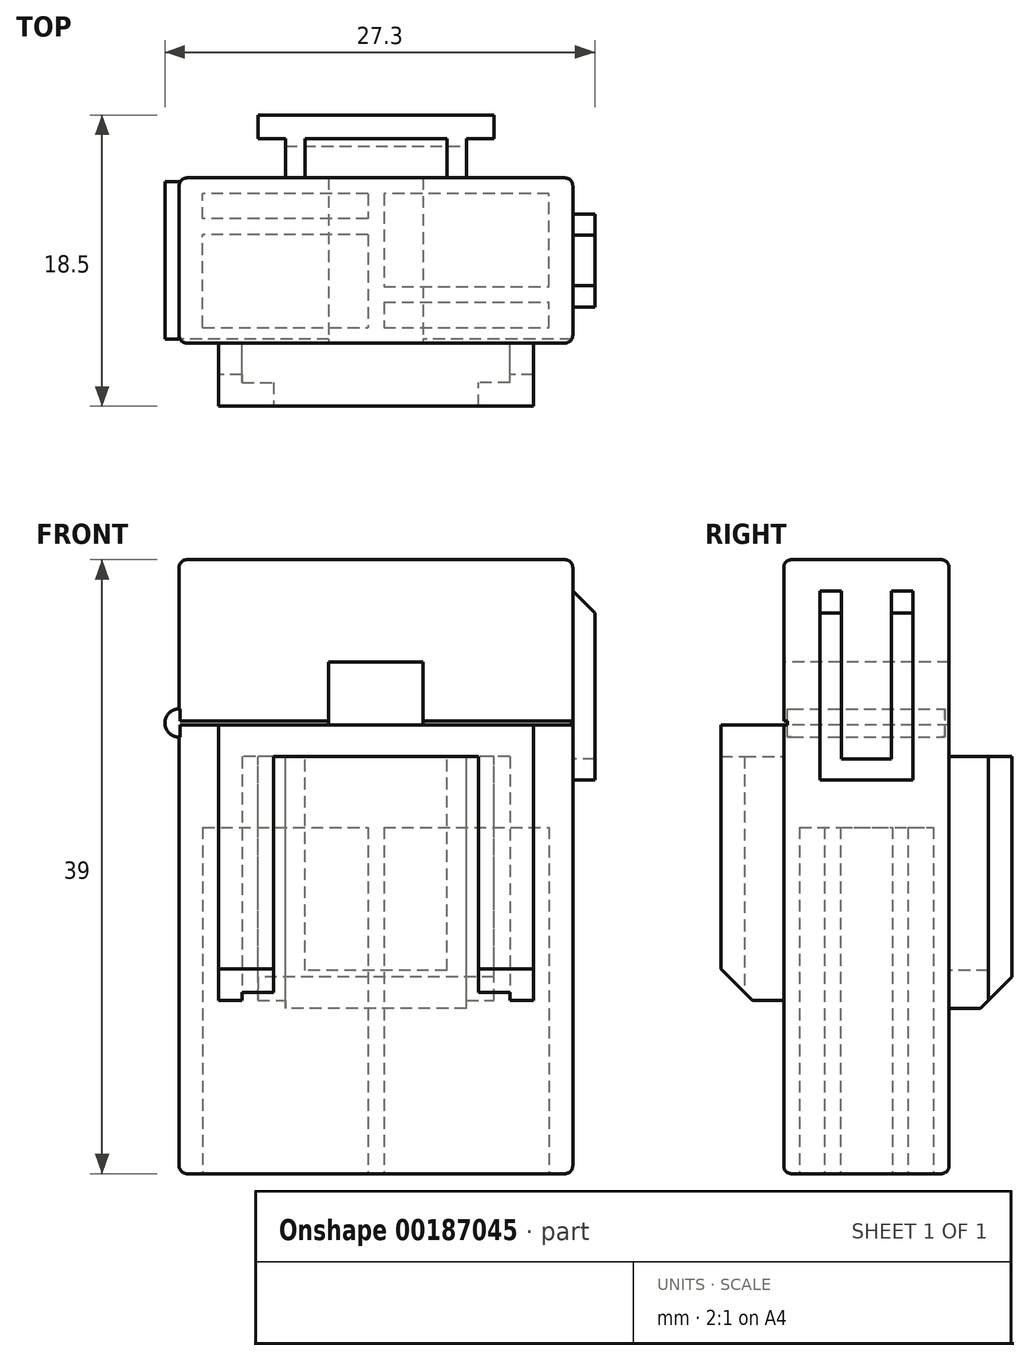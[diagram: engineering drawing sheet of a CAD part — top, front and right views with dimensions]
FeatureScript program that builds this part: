
annotation { "Feature Type Name" : "Feature", "Feature Type Description" : "" }
export const myFeature = defineFeature(function(context is Context, id is Id, definition is map)
    precondition{}
    {
        {
            var Q0;
            Q0=qCreatedBy(makeId("Front.planeOp"),FACE);
            var sketch = newSketch(context, id + "F0", { "sketchPlane" : qUnion([Q0])});
            skLineSegment(sketch, "E0.bottom", {"start": v(12.5, 19.5) * mm, "end": v(-12.5, 19.5) * mm});
            skLineSegment(sketch, "E0.top", {"start": v(12.5, -19.5) * mm, "end": v(-12.5, -19.5) * mm});
            skLineSegment(sketch, "E0.left", {"start": v(12.5, 19.5) * mm, "end": v(12.5, -19.5) * mm});
            skLineSegment(sketch, "E0.right", {"start": v(-12.5, 19.5) * mm, "end": v(-12.5, -19.5) * mm});
            skPoint(sketch, "E0.middle", {"position": v(0, 0) * mm});
            skSolve(sketch);
        }
        {
            var Q0;
            Q0=makeQuery(id+"F0.imprint","IMPRINT",FACE,{"disambiguationData":[TD([[makeQuery(id+"F0.imprint","IMPRINT",EDGE,{"derivedFrom":sQuery(id+"F0.wireOp",EDGE,"E0.bottom")}),1.0]])]});
            extrude(context, id + "F1", {"entities" : qUnion([Q0]), "endBound" : BoundingType.SYMMETRIC, "depth" : 10.5 * mm});
        }
        {
            var Q0;
            Q0=makeQuery(id+"F1.opExtrude","CAP_FACE",FACE,{"disambiguationData":[OSD([sQuery(id+"F0.wireOp",EDGE,"E0.bottom"),sQuery(id+"F0.wireOp",EDGE,"E0.top"),sQuery(id+"F0.wireOp",EDGE,"E0.left"),sQuery(id+"F0.wireOp",EDGE,"E0.right")])],"isStart":false});
            var sketch = newSketch(context, id + "F2", { "sketchPlane" : qUnion([Q0])});
            skLineSegment(sketch, "E1.0", {"start": v(10, 9) * mm, "end": v(-10, 9) * mm});
            skLineSegment(sketch, "E2.0", {"start": v(10, 9) * mm, "end": v(10, -8.5) * mm});
            skLineSegment(sketch, "E3.0", {"start": v(-10, 9) * mm, "end": v(-10, -8.5) * mm});
            skLineSegment(sketch, "E4.0", {"start": v(6.5, 7) * mm, "end": v(-6.5, 7) * mm});
            skLineSegment(sketch, "E5.0", {"start": v(6.5, 7) * mm, "end": v(6.5, -8.5) * mm});
            skLineSegment(sketch, "E6.0", {"start": v(-6.5, 7) * mm, "end": v(-6.5, -8.5) * mm});
            skLineSegment(sketch, "E7.0", {"start": v(10, -8.5) * mm, "end": v(6.5, -8.5) * mm});
            skLineSegment(sketch, "E8.trimOffspring", {"start": v(-6.5, -8.5) * mm, "end": v(-10, -8.5) * mm});
            skSolve(sketch);
        }
        {
            var Q0;
            Q0=makeQuery(id+"F2.imprint","IMPRINT",FACE,{"disambiguationData":[TD([[makeQuery(id+"F2.imprint","IMPRINT",EDGE,{"derivedFrom":sQuery(id+"F2.wireOp",EDGE,"E1.0")}),1.0]])]});
            extrude(context, id + "F3", {"entities" : qUnion([Q0]), "operationType" : NewBodyOperationType.ADD, "depth" : 4 * mm});
        }
        {
            var Q0;
            Q0=makeQuery(id+"F3.opExtrude","SWEPT_FACE",FACE,{"disambiguationData":[OSD([sQuery(id+"F2.wireOp",EDGE,"E7.0")])]});
            var sketch = newSketch(context, id + "F4", { "sketchPlane" : qUnion([Q0])});
            skLineSegment(sketch, "E9.0", {"start": v(8.5, 7.75) * mm, "end": v(8.5, 5.25) * mm});
            skLineSegment(sketch, "E10.0", {"start": v(8.5, 7.75) * mm, "end": v(6.5, 7.75) * mm});
            skLineSegment(sketch, "E11", {"start": v(6.5, 7.75) * mm, "end": v(6.5, 5.25) * mm});
            skLineSegment(sketch, "E12", {"start": v(6.5, 5.25) * mm, "end": v(8.5, 5.25) * mm});
            skLineSegment(sketch, "E13", {"start": v(8.5, 5.25) * mm, "end": v(6.5, 5.25) * mm});
            skLineSegment(sketch, "E14.MirrorCS", {"start": v(-8.5, 7.75) * mm, "end": v(-6.5, 7.75) * mm});
            skLineSegment(sketch, "E15.MirrorCS", {"start": v(-6.5, 7.75) * mm, "end": v(-6.5, 5.25) * mm});
            skLineSegment(sketch, "E16.MirrorCS", {"start": v(-8.5, 7.75) * mm, "end": v(-8.5, 5.25) * mm});
            skLineSegment(sketch, "E17.MirrorCS", {"start": v(-8.5, 5.25) * mm, "end": v(-6.5, 5.25) * mm});
            skSolve(sketch);
        }
        {
            var Q0;
            Q0=makeQuery(id+"F4.imprint","IMPRINT",FACE,{"disambiguationData":[TD([[makeQuery(id+"F4.imprint","IMPRINT",EDGE,{"derivedFrom":sQuery(id+"F4.wireOp",EDGE,"E9.0")}),-1.0]])]});
            var Q1;
            Q1=makeQuery(id+"F4.imprint","IMPRINT",FACE,{"disambiguationData":[TD([[makeQuery(id+"F4.imprint","IMPRINT",EDGE,{"derivedFrom":sQuery(id+"F4.wireOp",EDGE,"E14.MirrorCS")}),-1.0]])]});
            extrude(context, id + "F5", {"entities" : qUnion([Q0, Q1]), "operationType" : NewBodyOperationType.REMOVE, "oppositeDirection" : true, "depth" : 15.5 * mm});
        }
        {
            var Q0;
            Q0=makeQuery(id+"F5.boolean.opBoolean","MERGE",FACE,{"derivedFrom":[makeQuery(id+"F1.opExtrude","CAP_FACE",FACE,{"disambiguationData":[OSD([sQuery(id+"F0.wireOp",EDGE,"E0.bottom"),sQuery(id+"F0.wireOp",EDGE,"E0.top"),sQuery(id+"F0.wireOp",EDGE,"E0.left"),sQuery(id+"F0.wireOp",EDGE,"E0.right")])],"isStart":false}),makeQuery(id+"F5.opExtrude","SWEPT_FACE",FACE,{"disambiguationData":[OSD([sQuery(id+"F4.wireOp",EDGE,"E13")])]}),makeQuery(id+"F5.opExtrude","SWEPT_FACE",FACE,{"disambiguationData":[OSD([sQuery(id+"F4.wireOp",EDGE,"E17.MirrorCS")])]})]});
            var sketch = newSketch(context, id + "F6", { "sketchPlane" : qUnion([Q0])});
            skLineSegment(sketch, "E18.0", {"start": v(3, 13) * mm, "end": v(-3, 13) * mm});
            skLineSegment(sketch, "E19", {"start": v(0, 9) * mm, "end": v(0, 13) * mm});
            skLineSegment(sketch, "E20.0", {"start": v(3, 9) * mm, "end": v(3, 13) * mm});
            skLineSegment(sketch, "E21.MirrorCS", {"start": v(-3, 9) * mm, "end": v(-3, 13) * mm});
            skPoint(sketch, "E22.orphan", {"position": v(10, 13) * mm});
            skPoint(sketch, "E23.orphan", {"position": v(-10, 13) * mm});
            skLineSegment(sketch, "E24", {"start": v(-3, 9) * mm, "end": v(3, 9) * mm});
            skSolve(sketch);
        }
        {
            var Q0;
            {var subQ2=sQuery(id+"F6.wireOp",EDGE,"E19");Q0=makeQuery(id+"F6.imprint","IMPRINT",FACE,{"disambiguationData":[TD([[makeQuery(id+"F6.imprint","IMPRINT",EDGE,{"derivedFrom":subQ2}),-1.0]])]});}
            var Q1;
            {var subQ2=sQuery(id+"F6.wireOp",EDGE,"E19");Q1=makeQuery(id+"F6.imprint","IMPRINT",FACE,{"disambiguationData":[TD([[makeQuery(id+"F6.imprint","IMPRINT",EDGE,{"derivedFrom":subQ2}),1.0]])]});}
            extrude(context, id + "F7", {"entities" : qUnion([Q0, Q1]), "operationType" : NewBodyOperationType.REMOVE, "endBound" : BoundingType.THROUGH_ALL, "oppositeDirection" : true, "depth" : 25 * mm});
        }
        {
            var Q0;
            Q0=makeQuery(id+"F5.boolean.opBoolean","MERGE",FACE,{"derivedFrom":[makeQuery(id+"F1.opExtrude","CAP_FACE",FACE,{"disambiguationData":[OSD([sQuery(id+"F0.wireOp",EDGE,"E0.bottom"),sQuery(id+"F0.wireOp",EDGE,"E0.top"),sQuery(id+"F0.wireOp",EDGE,"E0.left"),sQuery(id+"F0.wireOp",EDGE,"E0.right")])],"isStart":false}),makeQuery(id+"F5.opExtrude","SWEPT_FACE",FACE,{"disambiguationData":[OSD([sQuery(id+"F4.wireOp",EDGE,"E13")])]}),makeQuery(id+"F5.opExtrude","SWEPT_FACE",FACE,{"disambiguationData":[OSD([sQuery(id+"F4.wireOp",EDGE,"E17.MirrorCS")])]})]});
            var sketch = newSketch(context, id + "F8", { "sketchPlane" : qUnion([Q0])});
            skLineSegment(sketch, "E25.0", {"start": v(12.5, 9) * mm, "end": v(-12.5, 9) * mm});
            skLineSegment(sketch, "E26.0", {"start": v(12.5, 9.25) * mm, "end": v(-12.5, 9.25) * mm});
            skLineSegment(sketch, "E27", {"start": v(12.5, 9.25) * mm, "end": v(12.5, 9) * mm});
            skLineSegment(sketch, "E28", {"start": v(-12.5, 9.25) * mm, "end": v(-12.5, 9) * mm});
            skSolve(sketch);
        }
        {
            var Q0;
            {var subQ0=sQuery(id+"F8.wireOp",EDGE,"E25.0");var subQ1=makeQuery(id+"F7.boolean.opBoolean","COPY",EDGE,{"derivedFrom":makeQuery(id+"F7.opExtrude","CAP_EDGE",EDGE,{"disambiguationData":[OSD([sQuery(id+"F6.wireOp",EDGE,"E20.0")])],"isStart":true})});var subQ2=makeQuery(id+"F8.imprint","INTERSECT",VERTEX,{"derivedFrom":[subQ1,subQ0]});Q0=makeQuery(id+"F8.imprint","IMPRINT",FACE,{"disambiguationData":[TD([[makeQuery(id+"F8.imprint","IMPRINT",EDGE,{"disambiguationData":[TD([[subQ2,-1.0]])],"derivedFrom":subQ0}),-1.0]])]});}
            var Q1;
            {var subQ0=sQuery(id+"F8.wireOp",EDGE,"E27");Q1=makeQuery(id+"F8.imprint","IMPRINT",FACE,{"disambiguationData":[TD([[makeQuery(id+"F8.imprint","IMPRINT",EDGE,{"derivedFrom":subQ0}),-1.0]])]});}
            var Q2;
            {var subQ0=sQuery(id+"F8.wireOp",EDGE,"E28");Q2=makeQuery(id+"F8.imprint","IMPRINT",FACE,{"disambiguationData":[TD([[makeQuery(id+"F8.imprint","IMPRINT",EDGE,{"derivedFrom":subQ0}),1.0]])]});}
            extrude(context, id + "F9", {"entities" : qUnion([Q0, Q1, Q2]), "operationType" : NewBodyOperationType.REMOVE, "oppositeDirection" : true, "depth" : 0.25 * mm});
        }
        {
            var Q0;
            Q0=makeQuery(id+"F1.opExtrude","SWEPT_FACE",FACE,{"disambiguationData":[OSD([sQuery(id+"F0.wireOp",EDGE,"E0.right")])]});
            var sketch = newSketch(context, id + "F10", { "sketchPlane" : qUnion([Q0])});
            skLineSegment(sketch, "E29", {"start": v(-5.25, 9.25) * mm, "end": v(5.25, 9.25) * mm});
            skLineSegment(sketch, "E30", {"start": v(5.25, 9.25) * mm, "end": v(5.25, 9) * mm});
            skLineSegment(sketch, "E31", {"start": v(5.25, 9) * mm, "end": v(-5.25, 9) * mm});
            skLineSegment(sketch, "E32", {"start": v(-5.25, 9) * mm, "end": v(-5.25, 9.25) * mm});
            skSolve(sketch);
        }
        {
            var Q0;
            {var subQ1=sQuery(id+"F8.wireOp",EDGE,"E28");var subQ2=makeQuery(id+"F9.boolean.opBoolean","COPY",EDGE,{"derivedFrom":makeQuery(id+"F9.opExtrude","CAP_EDGE",EDGE,{"disambiguationData":[OSD([subQ1])],"isStart":false})});Q0=makeQuery(id+"F10.imprint","IMPRINT",FACE,{"disambiguationData":[TD([[makeQuery(id+"F10.imprint","IMPRINT",EDGE,{"derivedFrom":subQ2}),-1.0]])]});}
            var Q1;
            {var subQ0=sQuery(id+"F10.wireOp",EDGE,"E32");Q1=makeQuery(id+"F10.imprint","IMPRINT",FACE,{"disambiguationData":[TD([[makeQuery(id+"F10.imprint","IMPRINT",EDGE,{"derivedFrom":subQ0}),-1.0]])]});}
            var Q2;
            {var subQ0=sQuery(id+"F10.wireOp",EDGE,"E30");Q2=makeQuery(id+"F10.imprint","IMPRINT",FACE,{"disambiguationData":[TD([[makeQuery(id+"F10.imprint","IMPRINT",EDGE,{"derivedFrom":subQ0}),-1.0]])]});}
            extrude(context, id + "F11", {"entities" : qUnion([Q0, Q1, Q2]), "operationType" : NewBodyOperationType.REMOVE, "oppositeDirection" : true, "depth" : 0.25 * mm});
        }
        {
            var Q0;
            {var subQ2=sQuery(id+"F0.wireOp",EDGE,"E0.left");var subQ3=sQuery(id+"F0.wireOp",EDGE,"E0.top");Q0=makeQuery(id+"Fof9NrGZvTUj0Qb_1.1.F11.boolean.opBoolean","SPLIT",FACE,{"disambiguationData":[TD([makeQuery(id+"F1.opExtrude","SWEPT_FACE",FACE,{"disambiguationData":[OSD([subQ3])]})])],"derivedFrom":makeQuery(id+"F1.opExtrude","SWEPT_FACE",FACE,{"disambiguationData":[OSD([subQ2])]})});}
            var sketch = newSketch(context, id + "F12", { "sketchPlane" : qUnion([Q0])});
            skLineSegment(sketch, "E33.0", {"start": v(-2.95, 17.5) * mm, "end": v(-1.6, 17.5) * mm});
            skLineSegment(sketch, "E34.0", {"start": v(-2.95, 5.5) * mm, "end": v(2.95, 5.5) * mm});
            skLineSegment(sketch, "E35.0", {"start": v(2.95, 17.5) * mm, "end": v(2.95, 5.5) * mm});
            skLineSegment(sketch, "E36.0", {"start": v(-2.95, 17.5) * mm, "end": v(-2.95, 5.5) * mm});
            skLineSegment(sketch, "E37.0", {"start": v(1.6, 17.5) * mm, "end": v(1.6, 6.85) * mm});
            skLineSegment(sketch, "E38.0", {"start": v(-1.6, 19.5) * mm, "end": v(-1.6, 6.85) * mm});
            skLineSegment(sketch, "E39.trimOffspring", {"start": v(1.6, 17.5) * mm, "end": v(2.95, 17.5) * mm});
            skLineSegment(sketch, "E40.trimOffspring", {"start": v(-1.6, 6.85) * mm, "end": v(1.6, 6.85) * mm});
            skSolve(sketch);
        }
        {
            var Q0;
            {var subQ0=sQuery(id+"F12.wireOp",EDGE,"E33.0");Q0=makeQuery(id+"F12.imprint","IMPRINT",FACE,{"disambiguationData":[TD([[makeQuery(id+"F12.imprint","IMPRINT",EDGE,{"derivedFrom":subQ0}),-1.0]])]});}
            var Q1;
            {var subQ0=sQuery(id+"F12.wireOp",EDGE,"E39.trimOffspring");Q1=makeQuery(id+"F12.imprint","IMPRINT",FACE,{"disambiguationData":[TD([[makeQuery(id+"F12.imprint","IMPRINT",EDGE,{"derivedFrom":subQ0}),-1.0]])]});}
            var Q2;
            {var subQ8=sQuery(id+"F12.wireOp",EDGE,"E34.0");Q2=makeQuery(id+"F12.imprint","IMPRINT",FACE,{"disambiguationData":[TD([[makeQuery(id+"F12.imprint","IMPRINT",EDGE,{"derivedFrom":subQ8}),1.0]])]});}
            extrude(context, id + "F13", {"entities" : qUnion([Q0, Q1, Q2]), "operationType" : NewBodyOperationType.ADD, "depth" : 1.4 * mm});
        }
        {
            var Q0;
            {var subQ1=sQuery(id+"F0.wireOp",EDGE,"E0.right");var subQ4=sQuery(id+"F0.wireOp",EDGE,"E0.bottom");var subQ7=makeQuery(id+"F1.opExtrude","SWEPT_FACE",FACE,{"disambiguationData":[OSD([subQ1])]});Q0=makeQuery(id+"F11.boolean.opBoolean","SPLIT",FACE,{"disambiguationData":[TD([makeQuery(id+"F1.opExtrude","SWEPT_FACE",FACE,{"disambiguationData":[OSD([subQ4])]})])],"derivedFrom":subQ7});}
            var sketch = newSketch(context, id + "F14", { "sketchPlane" : qUnion([Q0])});
            skLineSegment(sketch, "E41", {"start": v(-5.25, 9.25) * mm, "end": v(-5, 9.25) * mm});
            skLineSegment(sketch, "E42", {"start": v(-5, 9.25) * mm, "end": v(-5, 9) * mm});
            skLineSegment(sketch, "E43", {"start": v(-5, 9.13) * mm, "end": v(5, 9.13) * mm});
            skLineSegment(sketch, "E44.0", {"start": v(-5, 8.23) * mm, "end": v(5, 8.23) * mm});
            skLineSegment(sketch, "E45", {"start": v(5, 8.23) * mm, "end": v(5, 9.13) * mm});
            skLineSegment(sketch, "E46", {"start": v(-5, 9.13) * mm, "end": v(-5, 8.23) * mm});
            skSolve(sketch);
        }
        {
            var Q0;
            Q0 = qSketchRegion(id + "F14", true);
            var Q1;
            Q1=sQuery(id+"F14.wireOp",EDGE,"E43");
            revolve(context, id + "F15", {"operationType" : NewBodyOperationType.ADD, "entities" : qUnion([Q0]), "axis" : qUnion([Q1]), "revolveType" : RevolveType.FULL});
        }
        {
            var Q0;
            Q0=makeQuery(id+"F1.opExtrude","SWEPT_FACE",FACE,{"disambiguationData":[OSD([sQuery(id+"F0.wireOp",EDGE,"E0.bottom")])]});
            cPlane(context, id + "F16", {"entities" : qUnion([Q0]), "cplaneType" : CPlaneType.OFFSET, "offset" : 12.5 * mm, "oppositeDirection" : true, "width" : 150 * mm, "height" : 150 * mm});
        }
        {
            var Q0;
            Q0=qCreatedBy(id+"F16.planeOp",FACE);
            var sketch = newSketch(context, id + "F17", { "sketchPlane" : qUnion([Q0])});
            skLineSegment(sketch, "E47.0", {"start": v(7.5, 9.25) * mm, "end": v(-7.5, 9.25) * mm});
            skLineSegment(sketch, "E48.0", {"start": v(7.5, 7.75) * mm, "end": v(4.5, 7.75) * mm});
            skLineSegment(sketch, "E49.0", {"start": v(5.75, 5.25) * mm, "end": v(4.5, 5.25) * mm});
            skLineSegment(sketch, "E50.0", {"start": v(-7.5, 9.25) * mm, "end": v(-7.5, 7.75) * mm});
            skLineSegment(sketch, "E51.0", {"start": v(-5.75, 7.75) * mm, "end": v(-5.75, 5.25) * mm});
            skLineSegment(sketch, "E52.MirrorCS", {"start": v(7.5, 9.25) * mm, "end": v(7.5, 7.75) * mm});
            skLineSegment(sketch, "E53.MirrorCS", {"start": v(5.75, 7.75) * mm, "end": v(5.75, 5.25) * mm});
            skLineSegment(sketch, "E54.0", {"start": v(-4.5, 7.75) * mm, "end": v(-4.5, 5.25) * mm});
            skLineSegment(sketch, "E55.MirrorCS", {"start": v(4.5, 7.75) * mm, "end": v(4.5, 5.25) * mm});
            skPoint(sketch, "E56.orphan", {"position": v(7.5, 5.25) * mm});
            skPoint(sketch, "E57.orphan", {"position": v(-7.5, 5.25) * mm});
            skPoint(sketch, "E58.orphan", {"position": v(-4.5, 9.25) * mm});
            skPoint(sketch, "E59.orphan", {"position": v(-5.75, 9.25) * mm});
            skPoint(sketch, "E60.orphan", {"position": v(4.5, 9.25) * mm});
            skPoint(sketch, "E61.orphan", {"position": v(5.75, 9.25) * mm});
            skLineSegment(sketch, "E62.trimOffspring", {"start": v(-4.5, 7.75) * mm, "end": v(-7.5, 7.75) * mm});
            skPoint(sketch, "E63.orphan", {"position": v(12.5, 5.25) * mm});
            skPoint(sketch, "E64.trimOffspring.end.orphan", {"position": v(-12.5, 5.25) * mm});
            skPoint(sketch, "E65.orphan", {"position": v(-12.5, 9.25) * mm});
            skPoint(sketch, "E66.orphan", {"position": v(12.5, 9.25) * mm});
            skLineSegment(sketch, "E67.trimOffspring", {"start": v(-4.5, 5.25) * mm, "end": v(-5.75, 5.25) * mm});
            skLineSegment(sketch, "E68", {"start": v(-4.5, 7.75) * mm, "end": v(4.5, 7.75) * mm});
            skLineSegment(sketch, "E69", {"start": v(4.5, 5.25) * mm, "end": v(-4.5, 5.25) * mm});
            skPoint(sketch, "E70.orphan", {"position": v(0, 9.25) * mm});
            skPoint(sketch, "E71.end.orphan", {"position": v(0, 5.25) * mm});
            skSolve(sketch);
        }
        {
            var Q0;
            Q0=makeQuery(id+"F17.imprint","IMPRINT",FACE,{"disambiguationData":[TD([[makeQuery(id+"F17.imprint","IMPRINT",EDGE,{"derivedFrom":sQuery(id+"F17.wireOp",EDGE,"E47.0")}),1.0]])]});
            var Q1;
            Q1=makeQuery(id+"F17.imprint","IMPRINT",FACE,{"disambiguationData":[TD([[makeQuery(id+"F17.imprint","IMPRINT",EDGE,{"derivedFrom":sQuery(id+"F17.wireOp",EDGE,"E54.0")}),1.0]])]});
            var Q2;
            {var subQ0=sQuery(id+"F17.wireOp",EDGE,"E51.0");Q2=makeQuery(id+"F17.imprint","IMPRINT",FACE,{"disambiguationData":[TD([[makeQuery(id+"F17.imprint","IMPRINT",EDGE,{"derivedFrom":subQ0}),1.0]])]});}
            var Q3;
            Q3=makeQuery(id+"F17.imprint","IMPRINT",FACE,{"disambiguationData":[TD([[makeQuery(id+"F17.imprint","IMPRINT",EDGE,{"derivedFrom":sQuery(id+"F17.wireOp",EDGE,"E49.0")}),-1.0]])]});
            extrude(context, id + "F18", {"entities" : qUnion([Q0, Q1, Q2, Q3]), "operationType" : NewBodyOperationType.ADD, "oppositeDirection" : true, "depth" : 16 * mm});
        }
        {
            var Q0;
            Q0=makeQuery(id+"F17.imprint","IMPRINT",FACE,{"disambiguationData":[TD([[makeQuery(id+"F17.imprint","IMPRINT",EDGE,{"derivedFrom":sQuery(id+"F17.wireOp",EDGE,"E54.0")}),1.0]])]});
            extrude(context, id + "F19", {"entities" : qUnion([Q0]), "operationType" : NewBodyOperationType.REMOVE, "oppositeDirection" : true, "depth" : 13.6 * mm});
        }
        {
            var Q0;
            Q0=makeQuery(id+"F1.opExtrude","SWEPT_FACE",FACE,{"disambiguationData":[OSD([sQuery(id+"F0.wireOp",EDGE,"E0.bottom")])]});
            var Q1;
            {var subQ0=sQuery(id+"F0.wireOp",EDGE,"E0.right");var subQ1=sQuery(id+"F0.wireOp",EDGE,"E0.bottom");Q1=makeQuery(id+"F9.boolean.opBoolean","SPLIT",EDGE,{"disambiguationData":[TD([makeQuery(id+"F1.opExtrude","SWEPT_FACE",FACE,{"disambiguationData":[OSD([subQ1])]})])],"derivedFrom":makeQuery(id+"F1.opExtrude","CAP_EDGE",EDGE,{"disambiguationData":[OSD([subQ0])],"isStart":false})});}
            var Q2;
            {var subQ0=sQuery(id+"F0.wireOp",EDGE,"E0.left");var subQ1=sQuery(id+"F0.wireOp",EDGE,"E0.bottom");Q2=makeQuery(id+"F9.boolean.opBoolean","SPLIT",EDGE,{"disambiguationData":[TD([makeQuery(id+"F1.opExtrude","SWEPT_FACE",FACE,{"disambiguationData":[OSD([subQ1])]})])],"derivedFrom":makeQuery(id+"F1.opExtrude","CAP_EDGE",EDGE,{"disambiguationData":[OSD([subQ0])],"isStart":false})});}
            var Q3;
            {var subQ0=sQuery(id+"F0.wireOp",EDGE,"E0.bottom");var subQ1=sQuery(id+"F0.wireOp",EDGE,"E0.right");Q3=makeQuery(id+"FXFLqekEVwALpLj_1.1.F9.boolean.opBoolean","SPLIT",EDGE,{"disambiguationData":[TD([makeQuery(id+"F1.opExtrude","SWEPT_FACE",FACE,{"disambiguationData":[OSD([subQ0])]})])],"derivedFrom":makeQuery(id+"F1.opExtrude","CAP_EDGE",EDGE,{"disambiguationData":[OSD([subQ1])],"isStart":true})});}
            var Q4;
            {var subQ0=sQuery(id+"F0.wireOp",EDGE,"E0.bottom");var subQ1=sQuery(id+"F0.wireOp",EDGE,"E0.left");Q4=makeQuery(id+"FXFLqekEVwALpLj_1.1.F9.boolean.opBoolean","SPLIT",EDGE,{"disambiguationData":[TD([makeQuery(id+"F1.opExtrude","SWEPT_FACE",FACE,{"disambiguationData":[OSD([subQ0])]})])],"derivedFrom":makeQuery(id+"F1.opExtrude","CAP_EDGE",EDGE,{"disambiguationData":[OSD([subQ1])],"isStart":true})});}
            var Q5;
            {var subQ0=sQuery(id+"F0.wireOp",EDGE,"E0.right");var subQ1=sQuery(id+"F0.wireOp",EDGE,"E0.top");Q5=makeQuery(id+"FXFLqekEVwALpLj_1.1.F9.boolean.opBoolean","SPLIT",EDGE,{"disambiguationData":[TD([makeQuery(id+"F1.opExtrude","SWEPT_FACE",FACE,{"disambiguationData":[OSD([subQ1])]})])],"derivedFrom":makeQuery(id+"F1.opExtrude","CAP_EDGE",EDGE,{"disambiguationData":[OSD([subQ0])],"isStart":true})});}
            var Q6;
            {var subQ0=sQuery(id+"F0.wireOp",EDGE,"E0.right");var subQ1=sQuery(id+"F0.wireOp",EDGE,"E0.top");Q6=makeQuery(id+"F9.boolean.opBoolean","SPLIT",EDGE,{"disambiguationData":[TD([makeQuery(id+"F1.opExtrude","SWEPT_FACE",FACE,{"disambiguationData":[OSD([subQ1])]})])],"derivedFrom":makeQuery(id+"F1.opExtrude","CAP_EDGE",EDGE,{"disambiguationData":[OSD([subQ0])],"isStart":false})});}
            var Q7;
            {var subQ0=sQuery(id+"F0.wireOp",EDGE,"E0.left");var subQ2=sQuery(id+"F0.wireOp",EDGE,"E0.top");Q7=makeQuery(id+"FXFLqekEVwALpLj_1.1.F9.boolean.opBoolean","SPLIT",EDGE,{"disambiguationData":[TD([makeQuery(id+"F1.opExtrude","SWEPT_FACE",FACE,{"disambiguationData":[OSD([subQ2])]})])],"derivedFrom":makeQuery(id+"F1.opExtrude","CAP_EDGE",EDGE,{"disambiguationData":[OSD([subQ0])],"isStart":true})});}
            var Q8;
            {var subQ0=sQuery(id+"F0.wireOp",EDGE,"E0.left");var subQ1=sQuery(id+"F0.wireOp",EDGE,"E0.top");Q8=makeQuery(id+"F9.boolean.opBoolean","SPLIT",EDGE,{"disambiguationData":[TD([makeQuery(id+"F1.opExtrude","SWEPT_FACE",FACE,{"disambiguationData":[OSD([subQ1])]})])],"derivedFrom":makeQuery(id+"F1.opExtrude","CAP_EDGE",EDGE,{"disambiguationData":[OSD([subQ0])],"isStart":false})});}
            var Q9;
            Q9=makeQuery(id+"F1.opExtrude","CAP_EDGE",EDGE,{"disambiguationData":[OSD([sQuery(id+"F0.wireOp",EDGE,"E0.top")])],"isStart":true});
            var Q10;
            Q10=makeQuery(id+"F1.opExtrude","CAP_EDGE",EDGE,{"disambiguationData":[OSD([sQuery(id+"F0.wireOp",EDGE,"E0.top")])],"isStart":false});
            var Q11;
            Q11=makeQuery(id+"F1.opExtrude","SWEPT_EDGE",EDGE,{"disambiguationData":[OSD([sQuery(id+"F0.wireOp",EDGE,"E0.top"),sQuery(id+"F0.wireOp",EDGE,"E0.right")])]});
            var Q12;
            Q12=makeQuery(id+"F1.opExtrude","SWEPT_EDGE",EDGE,{"disambiguationData":[OSD([sQuery(id+"F0.wireOp",EDGE,"E0.top"),sQuery(id+"F0.wireOp",EDGE,"E0.left")])]});
            fillet(context, id + "F20", {"entities" : qUnion([Q0, Q1, Q2, Q3, Q4, Q5, Q6, Q7, Q8, Q9, Q10, Q11, Q12]), "radius" : 0.5 * mm, "tangentPropagation" : true, "allowEdgeOverflow" : false});
        }
        {
            var Q0;
            Q0=makeQuery(id+"F13.opExtrude","CAP_EDGE",EDGE,{"disambiguationData":[OSD([sQuery(id+"F12.wireOp",EDGE,"E39.trimOffspring")])],"isStart":false});
            var Q1;
            Q1=makeQuery(id+"F13.opExtrude","CAP_EDGE",EDGE,{"disambiguationData":[OSD([sQuery(id+"F12.wireOp",EDGE,"E33.0")])],"isStart":false});
            chamfer(context, id + "F21", {"entities" : qUnion([Q0, Q1]), "width" : 1.4 * mm, "tangentPropagation" : true});
        }
        {
            var Q0;
            Q0=makeQuery(id+"F3.opExtrude","CAP_EDGE",EDGE,{"disambiguationData":[OSD([sQuery(id+"F2.wireOp",EDGE,"E8.trimOffspring")])],"isStart":false});
            var Q1;
            Q1=makeQuery(id+"F3.opExtrude","CAP_EDGE",EDGE,{"disambiguationData":[OSD([sQuery(id+"F2.wireOp",EDGE,"E7.0")])],"isStart":false});
            chamfer(context, id + "F22", {"entities" : qUnion([Q0, Q1]), "width" : 2 * mm, "tangentPropagation" : true});
        }
        {
            var Q0;
            Q0=makeQuery(id+"F18.opExtrude","CAP_EDGE",EDGE,{"disambiguationData":[OSD([sQuery(id+"F17.wireOp",EDGE,"E47.0")])],"isStart":false});
            chamfer(context, id + "F23", {"entities" : qUnion([Q0]), "width" : 2 * mm, "tangentPropagation" : true});
        }
        {
            var Q0;
            Q0=makeQuery(id+"F1.opExtrude","SWEPT_FACE",FACE,{"disambiguationData":[OSD([sQuery(id+"F0.wireOp",EDGE,"E0.top")])]});
            var sketch = newSketch(context, id + "F24", { "sketchPlane" : qUnion([Q0])});
            skLineSegment(sketch, "E72.0", {"start": v(-11, 4.25) * mm, "end": v(-11, -1.65) * mm});
            skLineSegment(sketch, "E73.0", {"start": v(11, 4.25) * mm, "end": v(11, 2.65) * mm});
            skLineSegment(sketch, "E74.0", {"start": v(-11, 4.25) * mm, "end": v(-0.5, 4.25) * mm});
            skLineSegment(sketch, "E75.0", {"start": v(11, -4.25) * mm, "end": v(0.5, -4.25) * mm});
            skLineSegment(sketch, "E76.0", {"start": v(0.5, -4.25) * mm, "end": v(0.5, 1.65) * mm});
            skLineSegment(sketch, "E77.trimOffspring", {"start": v(0.5, 4.25) * mm, "end": v(11, 4.25) * mm});
            skLineSegment(sketch, "E78.trimOffspring", {"start": v(-0.5, -4.25) * mm, "end": v(-11, -4.25) * mm});
            skLineSegment(sketch, "E79.0", {"start": v(0.5, 2.65) * mm, "end": v(11, 2.65) * mm});
            skLineSegment(sketch, "E80.0", {"start": v(-0.5, -2.65) * mm, "end": v(-11, -2.65) * mm});
            skLineSegment(sketch, "E81.0", {"start": v(0.5, 1.65) * mm, "end": v(11, 1.65) * mm});
            skLineSegment(sketch, "E82.0", {"start": v(-0.5, -1.65) * mm, "end": v(-11, -1.65) * mm});
            skPoint(sketch, "E83.orphan", {"position": v(12, 4.25) * mm});
            skPoint(sketch, "E84.orphan", {"position": v(12, -4.25) * mm});
            skPoint(sketch, "E85.orphan", {"position": v(-12, 4.25) * mm});
            skPoint(sketch, "E86.orphan", {"position": v(-12, -4.25) * mm});
            skLineSegment(sketch, "E87.trimOffspring", {"start": v(-11, -2.65) * mm, "end": v(-11, -4.25) * mm});
            skLineSegment(sketch, "E88.trimOffspring", {"start": v(0.5, 2.65) * mm, "end": v(0.5, 4.25) * mm});
            skLineSegment(sketch, "E89.trimOffspring", {"start": v(11, 1.65) * mm, "end": v(11, -4.25) * mm});
            skLineSegment(sketch, "E90.0", {"start": v(-0.5, -1.65) * mm, "end": v(-0.5, 4.25) * mm});
            skLineSegment(sketch, "E91.0", {"start": v(-0.5, -4.25) * mm, "end": v(-0.5, -2.65) * mm});
            skPoint(sketch, "E92.orphan", {"position": v(0, -4.25) * mm});
            skPoint(sketch, "E93.orphan", {"position": v(0, 4.25) * mm});
            skSolve(sketch);
        }
        {
            var Q0;
            Q0=makeQuery(id+"F24.imprint","IMPRINT",FACE,{"disambiguationData":[TD([[makeQuery(id+"F24.imprint","IMPRINT",EDGE,{"derivedFrom":sQuery(id+"F24.wireOp",EDGE,"E72.0")}),1.0]])]});
            var Q1;
            Q1=makeQuery(id+"F24.imprint","IMPRINT",FACE,{"disambiguationData":[TD([[makeQuery(id+"F24.imprint","IMPRINT",EDGE,{"derivedFrom":sQuery(id+"F24.wireOp",EDGE,"E73.0")}),-1.0]])]});
            var Q2;
            Q2=makeQuery(id+"F24.imprint","IMPRINT",FACE,{"disambiguationData":[TD([[makeQuery(id+"F24.imprint","IMPRINT",EDGE,{"derivedFrom":sQuery(id+"F24.wireOp",EDGE,"E75.0")}),-1.0]])]});
            var Q3;
            Q3=makeQuery(id+"F24.imprint","IMPRINT",FACE,{"disambiguationData":[TD([[makeQuery(id+"F24.imprint","IMPRINT",EDGE,{"derivedFrom":sQuery(id+"F24.wireOp",EDGE,"E78.trimOffspring")}),-1.0]])]});
            extrude(context, id + "F25", {"entities" : qUnion([Q0, Q1, Q2, Q3]), "operationType" : NewBodyOperationType.REMOVE, "oppositeDirection" : true, "depth" : 22 * mm});
        }
    });
